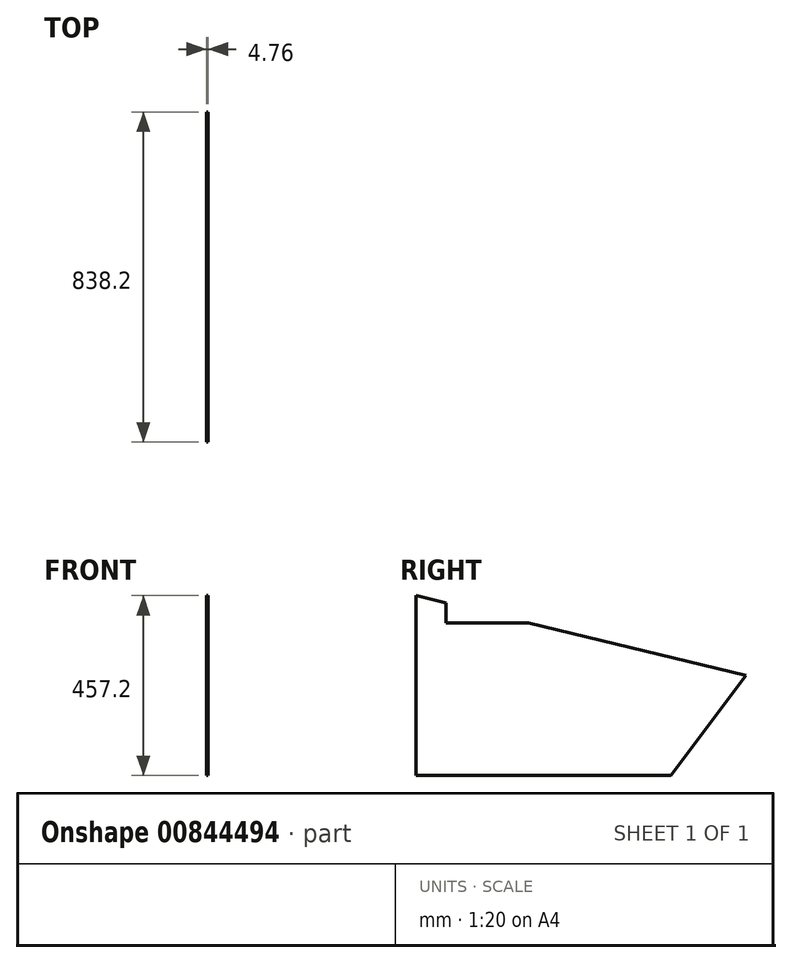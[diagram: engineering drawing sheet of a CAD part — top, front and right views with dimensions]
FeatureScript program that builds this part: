
annotation { "Feature Type Name" : "Feature", "Feature Type Description" : "" }
export const myFeature = defineFeature(function(context is Context, id is Id, definition is map)
    precondition{}
    {
        {
            var Q0;
            Q0=qCreatedBy(makeId("Right.planeOp"),FACE);
            var sketch = newSketch(context, id + "F0", { "sketchPlane" : qUnion([Q0])});
            skLineSegment(sketch, "E0", {"start": v(0, 0) * mm, "end": v(0, 457.2) * mm});
            skLineSegment(sketch, "E1", {"start": v(0, 457.2) * mm, "end": v(838.2, 254) * mm});
            skLineSegment(sketch, "E2", {"start": v(838.2, 254) * mm, "end": v(838.2, 0) * mm});
            skLineSegment(sketch, "E3", {"start": v(838.2, 0) * mm, "end": v(0, 0) * mm});
            skSolve(sketch);
        }
        {
            var Q0;
            Q0 = qSketchRegion(id + "F0", true);
            extrude(context, id + "F1", {"entities" : qUnion([Q0]), "depth" : 4.76 * mm, "offsetDistance" : 25.4 * mm});
        }
        {
            var Q0;
            Q0=makeQuery(id+"F1.opExtrude","CAP_FACE",FACE,{"disambiguationData":[OSD([sQuery(id+"F0.wireOp",EDGE,"E0"),sQuery(id+"F0.wireOp",EDGE,"E1"),sQuery(id+"F0.wireOp",EDGE,"E2"),sQuery(id+"F0.wireOp",EDGE,"E3")])],"isStart":true});
            var sketch = newSketch(context, id + "F2", { "sketchPlane" : qUnion([Q0])});
            skLineSegment(sketch, "E4", {"start": v(-76.2, 438.73) * mm, "end": v(-76.2, 387.93) * mm});
            skLineSegment(sketch, "E5", {"start": v(-76.2, 387.93) * mm, "end": v(-285.75, 387.93) * mm});
            skLineSegment(sketch, "E6", {"start": v(-285.75, 387.93) * mm, "end": v(-76.2, 438.73) * mm});
            skSolve(sketch);
        }
        {
            var Q0;
            Q0=makeQuery(id+"F2.imprint","IMPRINT",FACE,{"disambiguationData":[TD([[makeQuery(id+"F2.imprint","IMPRINT",EDGE,{"derivedFrom":sQuery(id+"F2.wireOp",EDGE,"E4")}),-1.0]])]});
            extrude(context, id + "F3", {"entities" : qUnion([Q0]), "operationType" : NewBodyOperationType.REMOVE, "endBound" : BoundingType.THROUGH_ALL, "oppositeDirection" : true, "depth" : 25.4 * mm, "offsetDistance" : 25.4 * mm});
        }
        {
            var Q0;
            Q0=makeQuery(id+"F1.opExtrude","CAP_FACE",FACE,{"disambiguationData":[OSD([sQuery(id+"F0.wireOp",EDGE,"E0"),sQuery(id+"F0.wireOp",EDGE,"E1"),sQuery(id+"F0.wireOp",EDGE,"E2"),sQuery(id+"F0.wireOp",EDGE,"E3")])],"isStart":false});
            var sketch = newSketch(context, id + "F4", { "sketchPlane" : qUnion([Q0])});
            skLineSegment(sketch, "E7", {"start": v(838.2, 254) * mm, "end": v(647.7, 0) * mm});
            skLineSegment(sketch, "E8", {"start": v(647.7, 0) * mm, "end": v(838.2, 0) * mm});
            skLineSegment(sketch, "E9", {"start": v(838.2, 0) * mm, "end": v(838.2, 254) * mm});
            skSolve(sketch);
        }
        {
            var Q0;
            Q0 = qSketchRegion(id + "F4", true);
            extrude(context, id + "F5", {"entities" : qUnion([Q0]), "operationType" : NewBodyOperationType.REMOVE, "endBound" : BoundingType.THROUGH_ALL, "oppositeDirection" : true, "depth" : 25.4 * mm, "offsetDistance" : 25.4 * mm});
        }
    });
